# Revit family: Haworth_Pergola_Accessory_TetheredLedge_PRELIM
name_source: partatom
category: Furniture Systems
revit_build: Autodesk Revit 2018 (Build: 20170223_1515(x64)
units: mm (PartAtom-declared; Revit-internal decimal feet)

## family parameters
Always vertical = Yes
Cut with Voids When Loaded = No
OmniClass Number = 23.40.70.14.64.21
OmniClass Title = Systems Furniture
Part Type = Normal
Room Calculation Point = No
Round Connector Dimension = Use Diameter
Shared = No
Work Plane-Based = No

## types (3) — shared parameters
Actual Depth = 7"
Actual Height = 201/256"
Assembly Code = E2020200
Bracket Depth = 5 23/64"
Bracket Offset = 1 23/64"
Bracket Thickness = 5/32"
Description = Haworth - Pergola Tethered Ledge
Manufacturer = Haworth
Model = Haworth Pergola
Revision Number = 1
Size = Verify Final Dim. w/ Haworth
Standard Width = 48, 72, 96, 120, 144 in.
Sustainability Info = http://www.haworth.com
Trim Finish = Haworth _ Paint _ Undecided _ Pergola
URL = http://www.haworth.com
URL - Product = https://www.haworth.com
Warranty = http://www.haworth.com
Worksurface Finish = Haworth _ Laminate _ Undecided _ Pergola

## per-type parameters (varying)
| type | Actual Width | Half Bracket Width | Width |
| 24w | 24" | 9" | 24" |
| 36w | 36" | 15" | 36" |
| 48w | 48" | 21" | 48" |

## geometry (parser evidence)
native form markers: Sweep x3
no freeform markers — native parametric forms only
